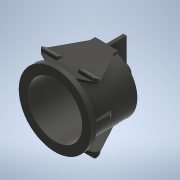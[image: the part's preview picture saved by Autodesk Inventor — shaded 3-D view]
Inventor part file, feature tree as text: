
AUTODESK INVENTOR PART (.ipt)
format: ipt  version: 2022.1 (Build 261234000, 234)  size: 283,136 bytes
history: native  units: mm
features: extrude x7, sketch x7, chamfer x3, other x2, mirror x2, projected_geometry x1
ambient origin geometry x8: Origin, YZ Plane, XZ Plane, XY Plane, X Axis, Y Axis, Z Axis, Center Point
bodies: body (feature_tree)
feature tree (22):
  other  "Твердое тело1"
  extrude  "Выдавливание1"  Depth=23.5mm
  extrude  "Выдавливание2"  Depth=18.0mm TaperAngle=0.0deg
  extrude  "Выдавливание3"  Depth=28.0mm
  extrude  "Выдавливание4"  Depth=2.0mm TaperAngle=0.0deg
  extrude  "Выдавливание5"  Depth=5.0mm
  chamfer  "Фаска1"  Distance=1.2mm
  other  "РабПлоскость1"
  extrude  "Выдавливание6"  Depth=2.5mm
  mirror  "Зеркальное отражение1"
  extrude  "Выдавливание8"  Depth=7.0mm TaperAngle=0.0deg
  chamfer  "Фаска2"  Distance=5.8mm
  chamfer  "Фаска3"  Distance=7.0mm
  mirror  "Зеркальное отражение2"
  sketch  "Эскиз1"
  sketch  "Эскиз2"
  sketch  "Эскиз3"
  sketch  "Эскиз4"
  sketch  "Эскиз5"
  sketch  "Эскиз7"
  sketch  "Эскиз9"
  projected_geometry  "Спроецированная петля1"
